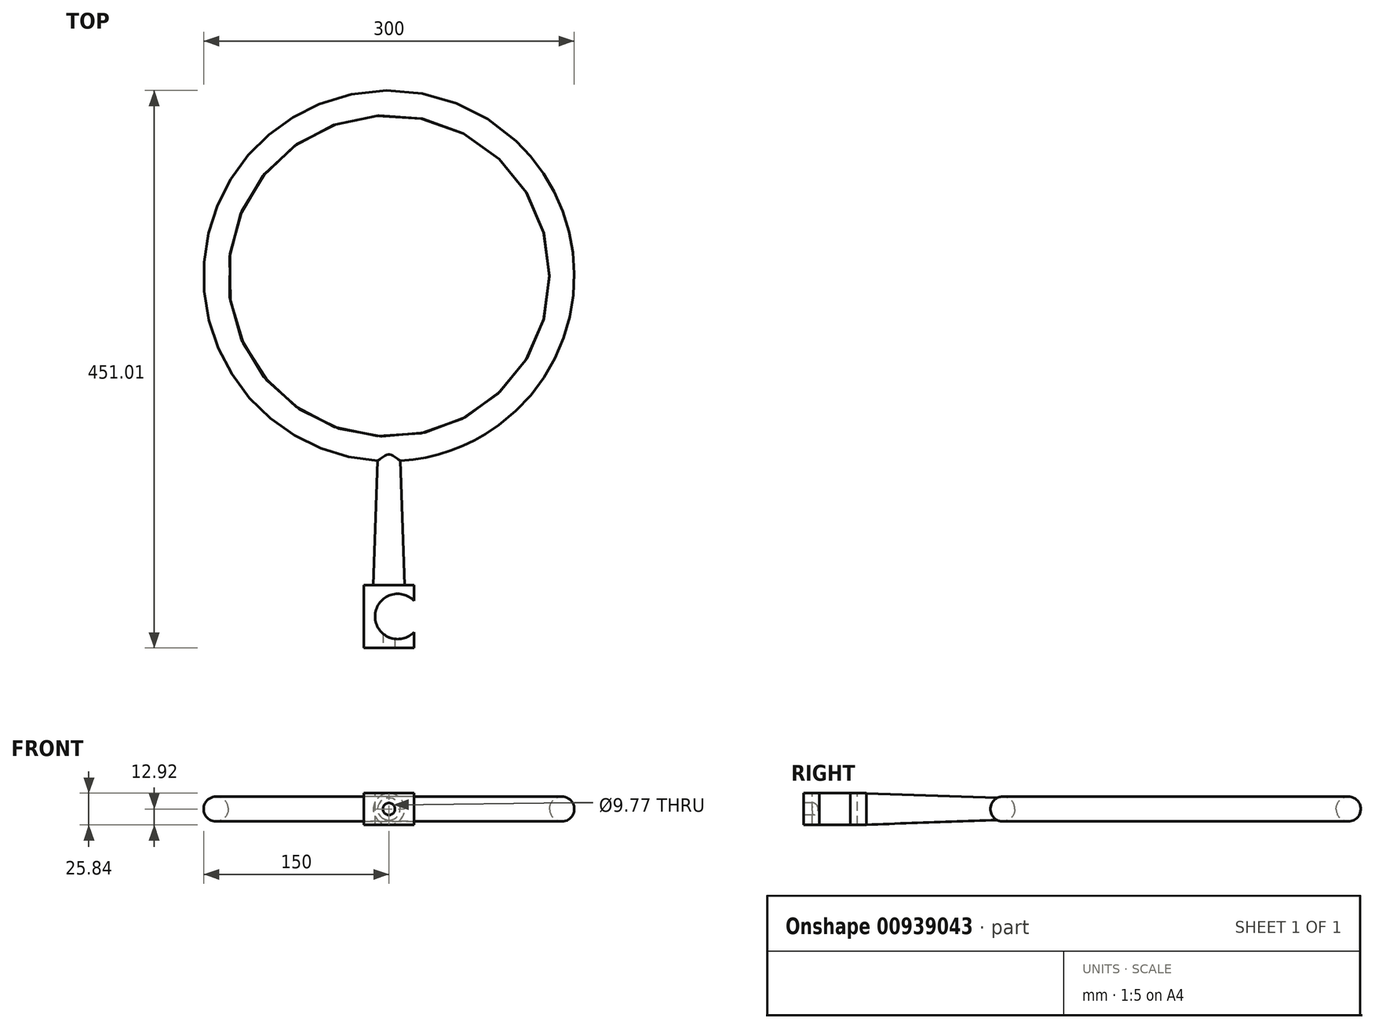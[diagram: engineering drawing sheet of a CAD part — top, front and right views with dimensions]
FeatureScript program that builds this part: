
annotation { "Feature Type Name" : "Feature", "Feature Type Description" : "" }
export const myFeature = defineFeature(function(context is Context, id is Id, definition is map)
    precondition{}
    {
        {
            var Q0;
            Q0=qCreatedBy(makeId("Front.planeOp"),FACE);
            var sketch = newSketch(context, id + "F0", { "sketchPlane" : qUnion([Q0])});
            skLineSegment(sketch, "E0", {"start": v(0, 0) * mm, "end": v(-140, 0) * mm});
            skCircle(sketch, "E1", {"center": v(-140, 0) * mm, "radius": 10 * mm});
            skLineSegment(sketch, "E2", {"start": v(0, 0) * mm, "end": v(0, 73.57) * mm});
            skSolve(sketch);
        }
        {
            var Q0;
            Q0 = qSketchRegion(id + "F0", true);
            var Q1;
            Q1=sQuery(id+"F0.wireOp",EDGE,"E2");
            revolve(context, id + "F1", {"surfaceOperationType" : NewSurfaceOperationType.NEW, "entities" : qUnion([Q0]), "axis" : qUnion([Q1]), "revolveType" : RevolveType.FULL});
        }
        {
            var Q0;
            Q0=qCreatedBy(makeId("Front.planeOp"),FACE);
            cPlane(context, id + "F2", {"entities" : qUnion([Q0]), "cplaneType" : CPlaneType.OFFSET, "offset" : 140.2 * mm, "width" : 152.4 * mm, "height" : 152.4 * mm});
        }
        {
            var Q0;
            Q0=qCreatedBy(id+"F2.planeOp",FACE);
            var sketch = newSketch(context, id + "F3", { "sketchPlane" : qUnion([Q0])});
            skCircle(sketch, "E3", {"center": v(0, 0) * mm, "radius": 8.8 * mm});
            skSolve(sketch);
        }
        {
            var Q0;
            Q0 = qSketchRegion(id + "F3", true);
            extrude(context, id + "F4", {"entities" : qUnion([Q0]), "operationType" : NewBodyOperationType.ADD, "depth" : 110 * mm, "offsetDistance" : 25.4 * mm, "hasDraft" : true, "draftAngle" : 2 * degree});
        }
        {
            var Q0;
            Q0=makeQuery(id+"F4.opExtrude","CAP_FACE",FACE,{"disambiguationData":[OSD([sQuery(id+"F3.wireOp",EDGE,"E3")])],"isStart":false});
            var sketch = newSketch(context, id + "F5", { "sketchPlane" : qUnion([Q0])});
            skLineSegment(sketch, "E4.bottom", {"start": v(20.45, 12.92) * mm, "end": v(-20.45, 12.92) * mm});
            skLineSegment(sketch, "E4.top", {"start": v(20.45, -12.92) * mm, "end": v(-20.45, -12.92) * mm});
            skLineSegment(sketch, "E4.left", {"start": v(20.45, 12.92) * mm, "end": v(20.45, -12.92) * mm});
            skLineSegment(sketch, "E4.right", {"start": v(-20.45, 12.92) * mm, "end": v(-20.45, -12.92) * mm});
            skPoint(sketch, "E4.middle", {"position": v(0, 0) * mm});
            skSolve(sketch);
        }
        {
            var Q0;
            Q0 = qSketchRegion(id + "F5", true);
            extrude(context, id + "F6", {"entities" : qUnion([Q0]), "operationType" : NewBodyOperationType.ADD, "depth" : 50.8 * mm, "offsetDistance" : 25.4 * mm});
        }
        {
            var Q0;
            Q0=makeQuery(id+"F6.opExtrude","SWEPT_FACE",FACE,{"disambiguationData":[OSD([sQuery(id+"F5.wireOp",EDGE,"E4.bottom")])]});
            var sketch = newSketch(context, id + "F7", { "sketchPlane" : qUnion([Q0])});
            skLineSegment(sketch, "E5", {"start": v(20.45, -275.6) * mm, "end": v(7.1, -275.6) * mm});
            skCircle(sketch, "E6", {"center": v(7.1, -275.6) * mm, "radius": 18.34 * mm});
            skSolve(sketch);
        }
        {
            var Q0;
            Q0 = qSketchRegion(id + "F7", true);
            extrude(context, id + "F8", {"entities" : qUnion([Q0]), "operationType" : NewBodyOperationType.REMOVE, "oppositeDirection" : true, "depth" : 38.1 * mm, "offsetDistance" : 25.4 * mm});
        }
        {
            var Q0;
            Q0=makeQuery(id+"F6.opExtrude","CAP_FACE",FACE,{"disambiguationData":[OSD([sQuery(id+"F5.wireOp",EDGE,"E4.bottom"),sQuery(id+"F5.wireOp",EDGE,"E4.top"),sQuery(id+"F5.wireOp",EDGE,"E4.left"),sQuery(id+"F5.wireOp",EDGE,"E4.right")])],"isStart":false});
            var sketch = newSketch(context, id + "F9", { "sketchPlane" : qUnion([Q0])});
            skCircle(sketch, "E7", {"center": v(0, 0) * mm, "radius": 4.88 * mm});
            skSolve(sketch);
        }
        {
            var Q0;
            Q0 = qSketchRegion(id + "F9", true);
            extrude(context, id + "F10", {"entities" : qUnion([Q0]), "operationType" : NewBodyOperationType.REMOVE, "oppositeDirection" : true, "depth" : 25.4 * mm, "offsetDistance" : 25.4 * mm});
        }
    });
